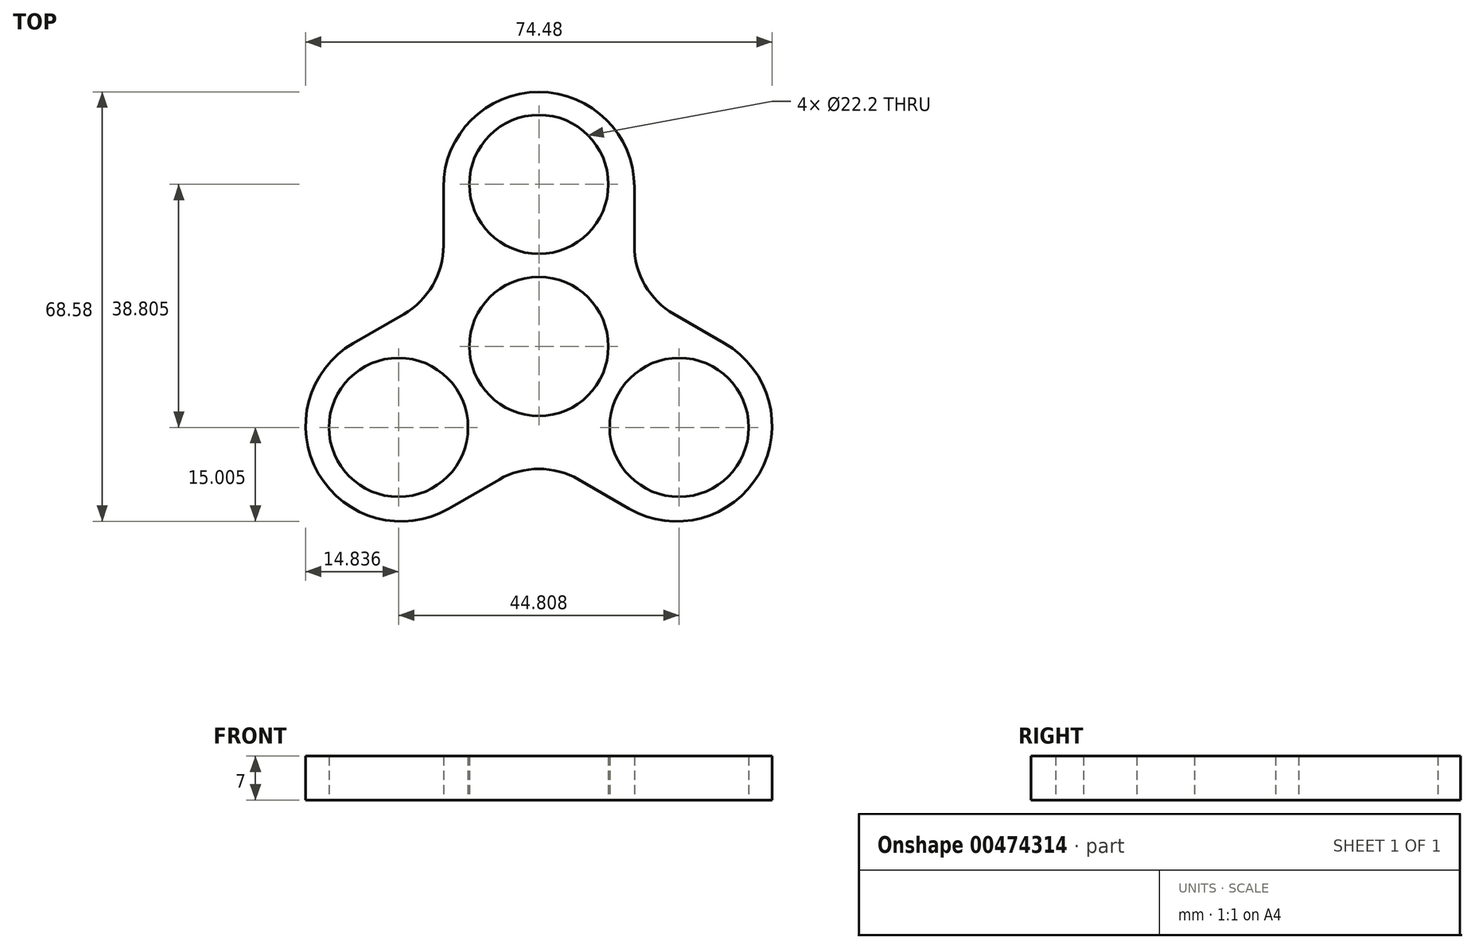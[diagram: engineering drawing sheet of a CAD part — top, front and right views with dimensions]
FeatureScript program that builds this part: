
annotation { "Feature Type Name" : "Feature", "Feature Type Description" : "" }
export const myFeature = defineFeature(function(context is Context, id is Id, definition is map)
    precondition{}
    {
        {
            var Q0;
            Q0=qCreatedBy(makeId("Top.planeOp"),FACE);
            var sketch = newSketch(context, id + "F0", { "sketchPlane" : qUnion([Q0])});
            skCircle(sketch, "E0", {"center": v(0, 0) * mm, "radius": 11.1 * mm});
            skLineSegment(sketch, "E1.top", {"start": v(-15.24, 40.64) * mm, "end": v(15.24, 40.64) * mm});
            skLineSegment(sketch, "E1.left", {"start": v(-15.24, 8.8) * mm, "end": v(-15.24, 40.64) * mm});
            skLineSegment(sketch, "E1.right", {"start": v(15.24, 8.8) * mm, "end": v(15.24, 40.64) * mm});
            skLineSegment(sketch, "E2", {"start": v(0, 11.1) * mm, "end": v(0, 40.64) * mm});
            skCircle(sketch, "E3", {"center": v(0, 25.87) * mm, "radius": 11.1 * mm});
            skLineSegment(sketch, "E4.1.0", {"start": v(-15.24, 8.8) * mm, "end": v(-42.82, -7.12) * mm});
            skCircle(sketch, "E4.1.1", {"center": v(-22.4, -12.93) * mm, "radius": 11.1 * mm});
            skLineSegment(sketch, "E4.1.2", {"start": v(0, -17.6) * mm, "end": v(-27.58, -33.52) * mm});
            skLineSegment(sketch, "E4.1.3", {"start": v(-27.58, -33.52) * mm, "end": v(-42.82, -7.12) * mm});
            skLineSegment(sketch, "E4.2.0", {"start": v(0, -17.6) * mm, "end": v(27.58, -33.52) * mm});
            skCircle(sketch, "E4.2.1", {"center": v(22.4, -12.94) * mm, "radius": 11.1 * mm});
            skLineSegment(sketch, "E4.2.2", {"start": v(15.24, 8.8) * mm, "end": v(42.82, -7.12) * mm});
            skLineSegment(sketch, "E4.2.3", {"start": v(42.82, -7.12) * mm, "end": v(27.58, -33.52) * mm});
            skPoint(sketch, "E5.orphan", {"position": v(-7.62, 13.2) * mm});
            skPoint(sketch, "E6.orphan", {"position": v(-15.24, 0) * mm});
            skPoint(sketch, "E1.bottom.end.orphan", {"position": v(15.24, 0) * mm});
            skSolve(sketch);
        }
        {
            var Q0;
            Q0=makeQuery(id+"F0.imprint","IMPRINT",FACE,{"disambiguationData":[TD([[makeQuery(id+"F0.imprint","IMPRINT",EDGE,{"derivedFrom":sQuery(id+"F0.wireOp",EDGE,"E0")}),-1.0]])]});
            extrude(context, id + "F1", {"entities" : qUnion([Q0]), "depth" : 7 * mm});
        }
        {
            var Q0;
            Q0=makeQuery(id+"F1.opExtrude","SWEPT_EDGE",EDGE,{"disambiguationData":[OSD([sQuery(id+"F0.wireOp",EDGE,"E1.top"),sQuery(id+"F0.wireOp",EDGE,"E1.right")])]});
            var Q1;
            Q1=makeQuery(id+"F1.opExtrude","SWEPT_EDGE",EDGE,{"disambiguationData":[OSD([sQuery(id+"F0.wireOp",EDGE,"E1.top"),sQuery(id+"F0.wireOp",EDGE,"E1.left")])]});
            var Q2;
            Q2=makeQuery(id+"F1.opExtrude","SWEPT_EDGE",EDGE,{"disambiguationData":[OSD([sQuery(id+"F0.wireOp",EDGE,"E4.1.0"),sQuery(id+"F0.wireOp",EDGE,"E4.1.3")])]});
            var Q3;
            Q3=makeQuery(id+"F1.opExtrude","SWEPT_EDGE",EDGE,{"disambiguationData":[OSD([sQuery(id+"F0.wireOp",EDGE,"E4.1.2"),sQuery(id+"F0.wireOp",EDGE,"E4.1.3")])]});
            var Q4;
            Q4=makeQuery(id+"F1.opExtrude","SWEPT_EDGE",EDGE,{"disambiguationData":[OSD([sQuery(id+"F0.wireOp",EDGE,"E4.2.2"),sQuery(id+"F0.wireOp",EDGE,"E4.2.3")])]});
            var Q5;
            Q5=makeQuery(id+"F1.opExtrude","SWEPT_EDGE",EDGE,{"disambiguationData":[OSD([sQuery(id+"F0.wireOp",EDGE,"E4.2.0"),sQuery(id+"F0.wireOp",EDGE,"E4.2.3")])]});
            fillet(context, id + "F2", {"entities" : qUnion([Q0, Q1, Q2, Q3, Q4, Q5]), "radius" : 15.24 * mm, "tangentPropagation" : true, "allowEdgeOverflow" : false});
        }
        {
            var Q0;
            Q0=makeQuery(id+"F1.opExtrude","SWEPT_EDGE",EDGE,{"disambiguationData":[OSD([sQuery(id+"F0.wireOp",EDGE,"E1.right"),sQuery(id+"F0.wireOp",EDGE,"E4.2.2")])]});
            var Q1;
            Q1=makeQuery(id+"F1.opExtrude","SWEPT_EDGE",EDGE,{"disambiguationData":[OSD([sQuery(id+"F0.wireOp",EDGE,"E4.1.2"),sQuery(id+"F0.wireOp",EDGE,"E4.2.0")])]});
            var Q2;
            Q2=makeQuery(id+"F1.opExtrude","SWEPT_EDGE",EDGE,{"disambiguationData":[OSD([sQuery(id+"F0.wireOp",EDGE,"E1.left"),sQuery(id+"F0.wireOp",EDGE,"E4.1.0")])]});
            fillet(context, id + "F3", {"entities" : qUnion([Q0, Q1, Q2]), "radius" : 12.7 * mm, "tangentPropagation" : true, "allowEdgeOverflow" : false});
        }
    });
